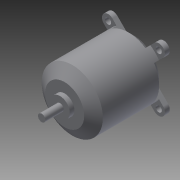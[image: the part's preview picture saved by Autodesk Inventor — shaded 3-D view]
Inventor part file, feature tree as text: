
AUTODESK INVENTOR PART (.ipt)
format: ipt  version: 2015 (Build 190159000, 159)  size: 167,936 bytes
history: native  units: in
note: dims shown in document units (in); Inventor stores cm internally (conversion verified against a paired STEP export)
features: sketch x5, extrude x2, other x2, chamfer x1, plane x1, revolve x1
ambient origin geometry x8: Origin, YZ Plane, XZ Plane, XY Plane, X Axis, Y Axis, Z Axis, Center Point
bodies: Solid1 (feature_tree)
feature tree (12):
  extrude  "Extrusion1"  TaperAngle=135.0deg  [1 undecoded]
  extrude  "Extrusion2"  TaperAngle=45.0deg  [1 undecoded]
  chamfer  "Chamfer1"  Distance=0.1969in
  sketch  "Sketch3"  dims[d4=0.0984in]
  other  "Work Axis1"
  other  "Work Point1"
  sketch  "Sketch4"  dims[d5=0.0984in]
  plane  "Work Plane1"
  revolve  "Revolution1"  [1 undecoded]
  sketch  "Sketch1"  dims[d0=1.1535in d1=135.0deg]
  sketch  "Sketch2"  dims[d2=1.1535in d3=45.0deg]
  sketch  "Sketch5"  dims[d6=0.1969in d7=0.1969in d8=0.1575in d9=0.0in d10=0.9846in d11=1.9685in d12=0.0in d13=0.1575in d14=0.0787in d15=45.0deg d16=0.9843in d17=0.1181in d18=0.5906in d19=0.1969in d20=0.1476in d21=0.315in d22=90.0deg]
note: 3 required parameter values undecoded (feature->parameter linkage not recoverable at this tier; creation-order binding heuristic only, values carry confidence <= 0.55)